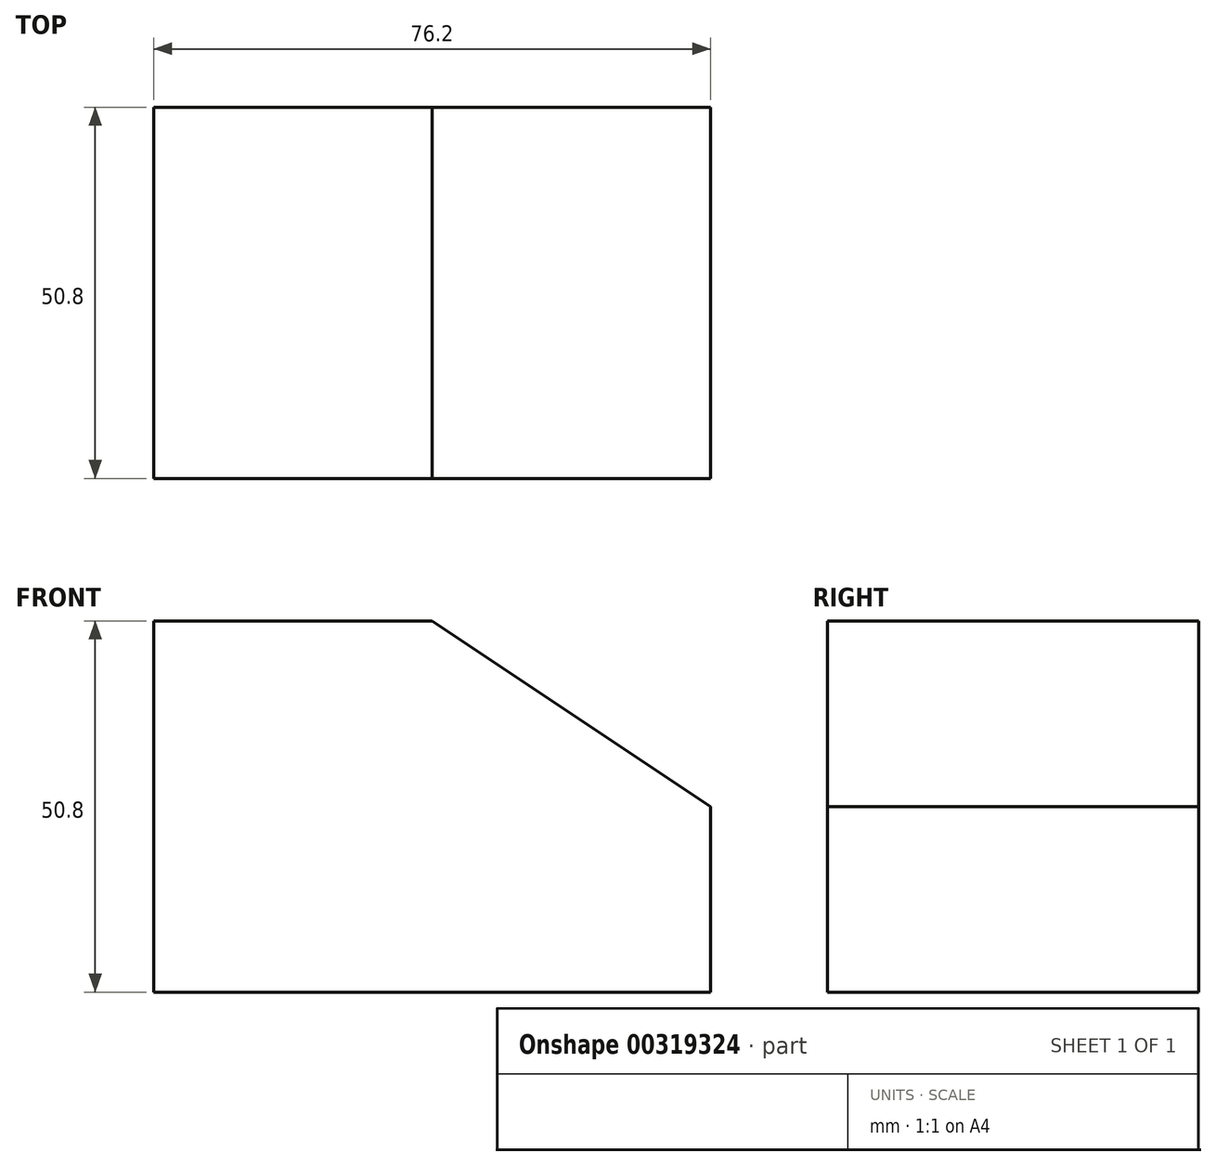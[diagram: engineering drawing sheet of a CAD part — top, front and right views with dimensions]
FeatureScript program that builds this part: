
annotation { "Feature Type Name" : "Feature", "Feature Type Description" : "" }
export const myFeature = defineFeature(function(context is Context, id is Id, definition is map)
    precondition{}
    {
        {
            var Q0;
            Q0=qCreatedBy(makeId("Front.planeOp"),FACE);
            var sketch = newSketch(context, id + "F0", { "sketchPlane" : qUnion([Q0])});
            skLineSegment(sketch, "E0", {"start": v(-43.83, 21.73) * mm, "end": v(-43.83, -29.07) * mm});
            skLineSegment(sketch, "E1", {"start": v(-43.83, 21.73) * mm, "end": v(-5.73, 21.73) * mm});
            skLineSegment(sketch, "E2", {"start": v(-5.73, 21.73) * mm, "end": v(-43.83, 21.73) * mm});
            skLineSegment(sketch, "E3", {"start": v(-43.83, -29.07) * mm, "end": v(32.37, -29.07) * mm});
            skLineSegment(sketch, "E4", {"start": v(32.37, -29.07) * mm, "end": v(32.37, -3.67) * mm});
            skLineSegment(sketch, "E5", {"start": v(32.37, -3.67) * mm, "end": v(-5.73, 21.73) * mm});
            skSolve(sketch);
        }
        {
            var Q0;
            Q0 = qSketchRegion(id + "F0", true);
            var Q1;
            Q1=makeQuery(id+"F0.imprint","IMPRINT",FACE,{"disambiguationData":[TD([[makeQuery(id+"F0.imprint","IMPRINT",EDGE,{"derivedFrom":sQuery(id+"F0.wireOp",EDGE,"E0")}),1.0]])]});
            extrude(context, id + "F1", {"entities" : qUnion([Q0, Q1]), "depth" : 50.8 * mm});
        }
    });
